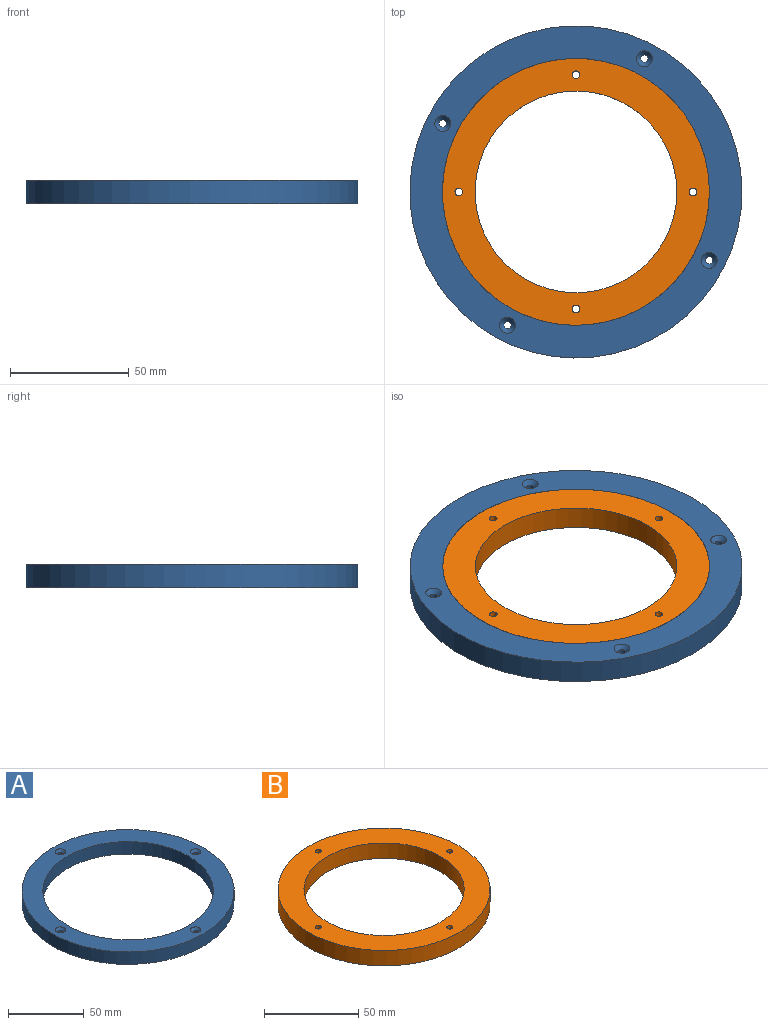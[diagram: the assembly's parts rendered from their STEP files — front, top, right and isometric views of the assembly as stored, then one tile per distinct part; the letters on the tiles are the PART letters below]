
ASSEMBLY  parts=2 mates=2
PART A: 12 faces, bbox 140x140x10 mm
  f0: cylinder r=56.25mm len=112.5mm, axis (0,0,-1), area 3534.3mm2, adj f2,f3
  f1: cylinder r=70mm len=140mm, axis (0,0,-1), area 4398.2mm2, adj f2,f3
  f2: plane 140x140mm, normal (0,0,1), area 5311.7mm2, adj f0,f1,f5,f7,f9,f11
  f3: plane 140x140mm, normal (0,0,-1), area 5421.4mm2, adj f0,f1,f4,f6,f8,f10
  f4: cylinder r=1.6mm len=8.24mm, axis (0,0,1), area 82.8mm2, adj f3,f5
  f5: cone r=1.6mm half-angle=45deg, axis (0,0,1), area 38.8mm2, adj f2,f4
  f6: cylinder r=1.6mm len=8.24mm, axis (0,0,1), area 82.8mm2, adj f3,f7
  f7: cone r=1.6mm half-angle=45deg, axis (0,0,1), area 38.8mm2, adj f2,f6
  f8: cylinder r=1.6mm len=8.24mm, axis (0,0,1), area 82.8mm2, adj f3,f9
  f9: cone r=1.6mm half-angle=45deg, axis (0,0,1), area 38.8mm2, adj f2,f8
  f10: cylinder r=1.6mm len=8.24mm, axis (0,0,1), area 82.8mm2, adj f3,f11
  f11: cone r=1.6mm half-angle=45deg, axis (0,0,1), area 38.8mm2, adj f2,f10
PART B: 12 faces, bbox 112.5x112.5x10 mm
  f0: cylinder r=42.5mm len=85mm, axis (0,0,-1), area 2670.4mm2, adj f2,f3
  f1: cylinder r=56.25mm len=112.5mm, axis (0,0,-1), area 3534.3mm2, adj f2,f3
  f2: plane 112.5x112.5mm, normal (0,0,1), area 4233.5mm2, adj f0,f1,f4,f6,f8,f10
  f3: plane 112.5x112.5mm, normal (0,0,-1), area 4123.8mm2, adj f0,f1,f5,f7,f9,f11
  f4: cylinder r=1.6mm len=8.24mm, axis (0,0,-1), area 82.8mm2, adj f2,f5
  f5: cone r=1.6mm half-angle=45deg, axis (0,0,-1), area 38.8mm2, adj f3,f4
  f6: cylinder r=1.6mm len=8.24mm, axis (0,0,-1), area 82.8mm2, adj f2,f7
  f7: cone r=1.6mm half-angle=45deg, axis (0,0,-1), area 38.8mm2, adj f3,f6
  f8: cylinder r=1.6mm len=8.24mm, axis (0,0,-1), area 82.8mm2, adj f2,f9
  f9: cone r=1.6mm half-angle=45deg, axis (0,0,-1), area 38.8mm2, adj f3,f8
  f10: cylinder r=1.6mm len=8.24mm, axis (0,0,-1), area 82.8mm2, adj f2,f11
  f11: cone r=1.6mm half-angle=45deg, axis (0,0,-1), area 38.8mm2, adj f3,f10
PLACE A rot(axis=(0,0,-1),27.2deg) t=(-0.43,2.56,4.2)mm
PLACE B t=(-0.43,2.56,4.2)mm fixed
MATE planar A.f1 <-> B.f1  axis (0,0,1) through (-0.43,2.56,9.2)mm
MATE cylindrical A.f1 <-> B.f1  axis (0,0,-1) through (-0.43,2.56,4.2)mm
